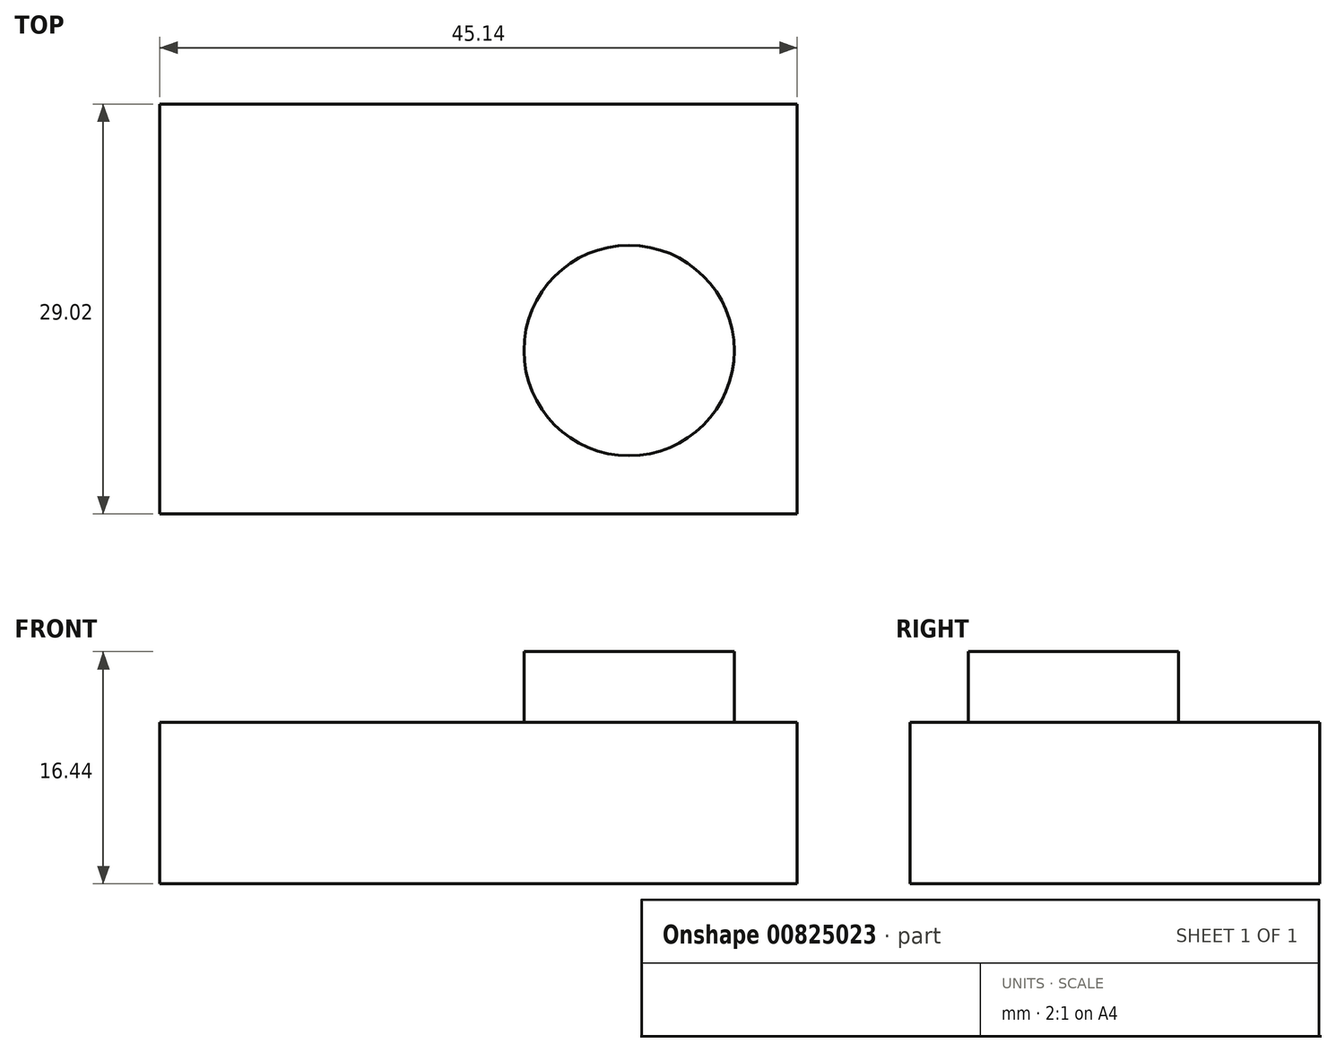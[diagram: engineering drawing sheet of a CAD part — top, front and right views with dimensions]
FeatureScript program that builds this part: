
annotation { "Feature Type Name" : "Feature", "Feature Type Description" : "" }
export const myFeature = defineFeature(function(context is Context, id is Id, definition is map)
    precondition{}
    {
        {
            var Q0;
            Q0=qCreatedBy(makeId("Top.planeOp"),FACE);
            var sketch = newSketch(context, id + "F0", { "sketchPlane" : qUnion([Q0])});
            skLineSegment(sketch, "E0", {"start": v(-31.83, 23.91) * mm, "end": v(-31.83, -5.1) * mm});
            skLineSegment(sketch, "E1", {"start": v(-31.83, -5.1) * mm, "end": v(13.3, -5.1) * mm});
            skLineSegment(sketch, "E2", {"start": v(13.3, -5.1) * mm, "end": v(13.3, 23.91) * mm});
            skLineSegment(sketch, "E3", {"start": v(13.3, 23.91) * mm, "end": v(-31.83, 23.91) * mm});
            skSolve(sketch);
        }
        {
            var Q0;
            Q0=makeQuery(id+"F0.imprint","IMPRINT",FACE,{"disambiguationData":[TD([[makeQuery(id+"F0.imprint","IMPRINT",EDGE,{"derivedFrom":sQuery(id+"F0.wireOp",EDGE,"E0")}),1.0]])]});
            extrude(context, id + "F1", {"entities" : qUnion([Q0]), "depth" : 11.44 * mm, "offsetDistance" : 25.4 * mm});
        }
        {
            var Q0;
            Q0=makeQuery(id+"F1.opExtrude","CAP_FACE",FACE,{"disambiguationData":[OSD([sQuery(id+"F0.wireOp",EDGE,"E0"),sQuery(id+"F0.wireOp",EDGE,"E1"),sQuery(id+"F0.wireOp",EDGE,"E2"),sQuery(id+"F0.wireOp",EDGE,"E3")])],"isStart":false});
            var sketch = newSketch(context, id + "F2", { "sketchPlane" : qUnion([Q0])});
            skCircle(sketch, "E4", {"center": v(1.4, 6.46) * mm, "radius": 7.45 * mm});
            skSolve(sketch);
        }
        {
            var Q0;
            Q0=makeQuery(id+"F2.imprint","IMPRINT",FACE,{"disambiguationData":[TD([[makeQuery(id+"F2.imprint","IMPRINT",EDGE,{"derivedFrom":sQuery(id+"F2.wireOp",EDGE,"E4")}),1.0]])]});
            extrude(context, id + "F3", {"entities" : qUnion([Q0]), "operationType" : NewBodyOperationType.ADD, "depth" : 5 * mm, "offsetDistance" : 25.4 * mm});
        }
    });
